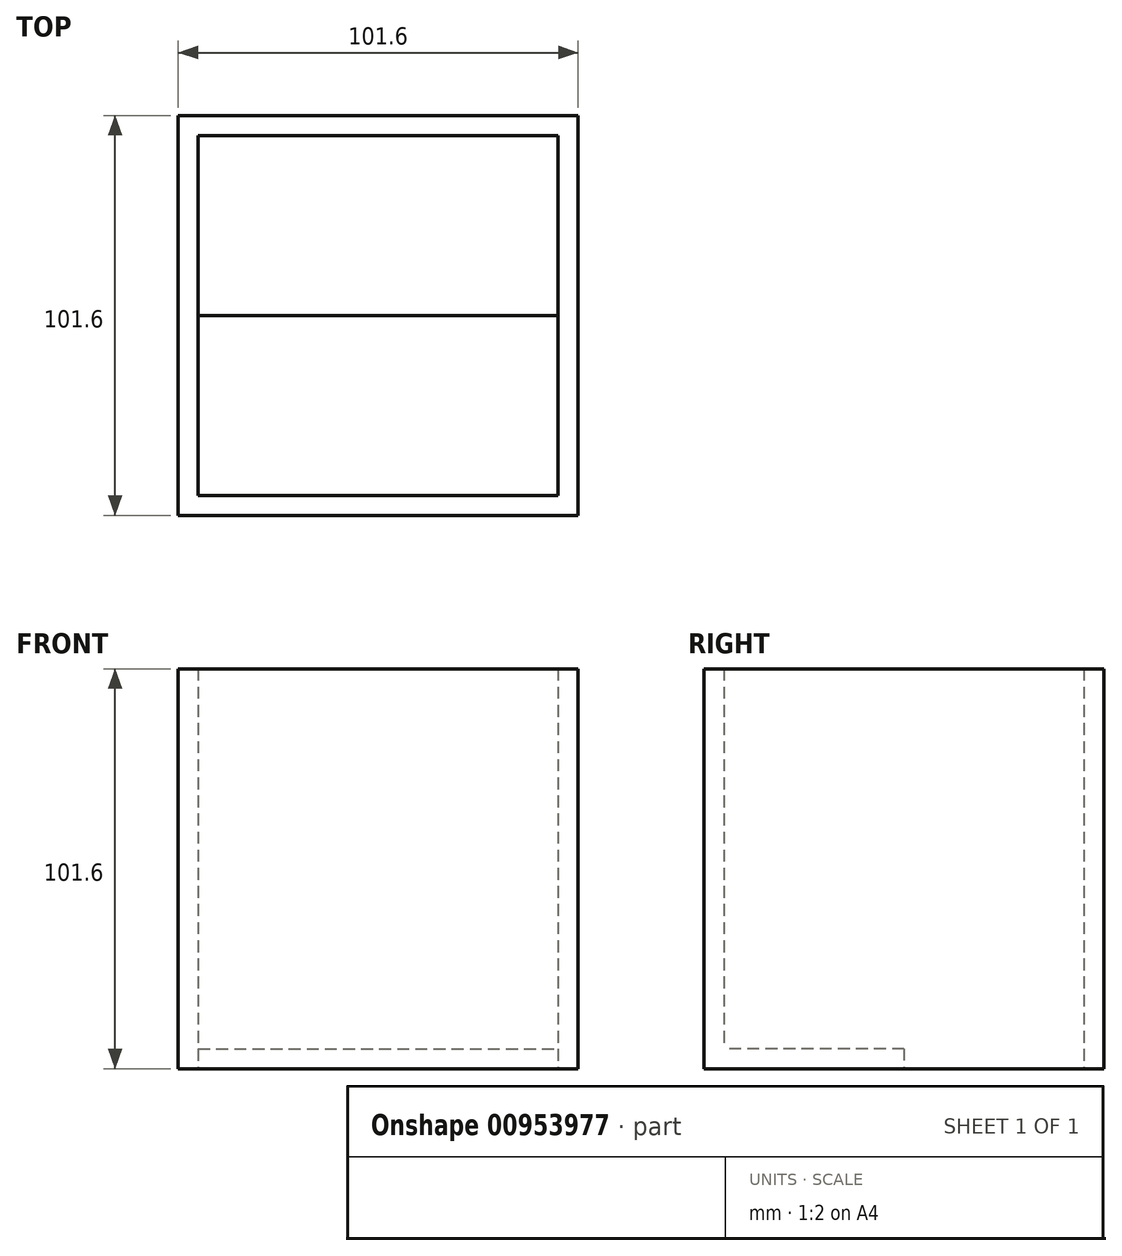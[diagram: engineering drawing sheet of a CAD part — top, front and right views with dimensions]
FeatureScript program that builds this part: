
annotation { "Feature Type Name" : "Feature", "Feature Type Description" : "" }
export const myFeature = defineFeature(function(context is Context, id is Id, definition is map)
    precondition{}
    {
        {
            var Q0;
            Q0=qCreatedBy(makeId("Top.planeOp"),FACE);
            var sketch = newSketch(context, id + "F0", { "sketchPlane" : qUnion([Q0])});
            skLineSegment(sketch, "E0.bottom", {"start": v(-50.8, 50.8) * mm, "end": v(50.8, 50.8) * mm});
            skLineSegment(sketch, "E0.top", {"start": v(-50.8, -50.8) * mm, "end": v(50.8, -50.8) * mm});
            skLineSegment(sketch, "E0.left", {"start": v(-50.8, 50.8) * mm, "end": v(-50.8, -50.8) * mm});
            skLineSegment(sketch, "E0.right", {"start": v(50.8, 50.8) * mm, "end": v(50.8, -50.8) * mm});
            skLineSegment(sketch, "E1.bottom", {"start": v(-45.72, 45.72) * mm, "end": v(45.72, 45.72) * mm});
            skLineSegment(sketch, "E1.top", {"start": v(-45.72, -45.72) * mm, "end": v(45.72, -45.72) * mm});
            skLineSegment(sketch, "E1.left", {"start": v(-45.72, 45.72) * mm, "end": v(-45.72, -45.72) * mm});
            skLineSegment(sketch, "E1.right", {"start": v(45.72, 45.72) * mm, "end": v(45.72, -45.72) * mm});
            skPoint(sketch, "E1.middle", {"position": v(0, 0) * mm});
            skSolve(sketch);
        }
        {
            var Q0;
            Q0=makeQuery(id+"F0.imprint","IMPRINT",FACE,{"disambiguationData":[TD([[makeQuery(id+"F0.imprint","IMPRINT",EDGE,{"derivedFrom":sQuery(id+"F0.wireOp",EDGE,"E1.bottom")}),-1.0]])]});
            var sketch = newSketch(context, id + "F1", { "sketchPlane" : qUnion([Q0])});
            skLineSegment(sketch, "E2", {"start": v(-50.68, 0) * mm, "end": v(50.98, 0) * mm});
            skSolve(sketch);
        }
        {
            var Q0;
            Q0 = qSketchRegion(id + "F1", true);
            var Q1;
            Q1=makeQuery(id+"F0.imprint","IMPRINT",FACE,{"disambiguationData":[TD([[makeQuery(id+"F0.imprint","IMPRINT",EDGE,{"derivedFrom":sQuery(id+"F0.wireOp",EDGE,"E0.bottom")}),-1.0]])]});
            extrude(context, id + "F2", {"entities" : qUnion([Q0, Q1]), "depth" : 101.6 * mm, "offsetDistance" : 25.4 * mm});
        }
        {
            var Q0;
            {var subQ5=makeQuery(id+"F0.imprint","IMPRINT",EDGE,{"derivedFrom":sQuery(id+"F0.wireOp",EDGE,"E1.top")});Q0=makeQuery(id+"F1.imprint","IMPRINT",FACE,{"disambiguationData":[TD([[makeQuery(id+"F1.imprint","IMPRINT",EDGE,{"derivedFrom":subQ5}),1.0]])]});}
            extrude(context, id + "F3", {"entities" : qUnion([Q0]), "operationType" : NewBodyOperationType.ADD, "depth" : 5.08 * mm, "offsetDistance" : 25.4 * mm});
        }
    });
